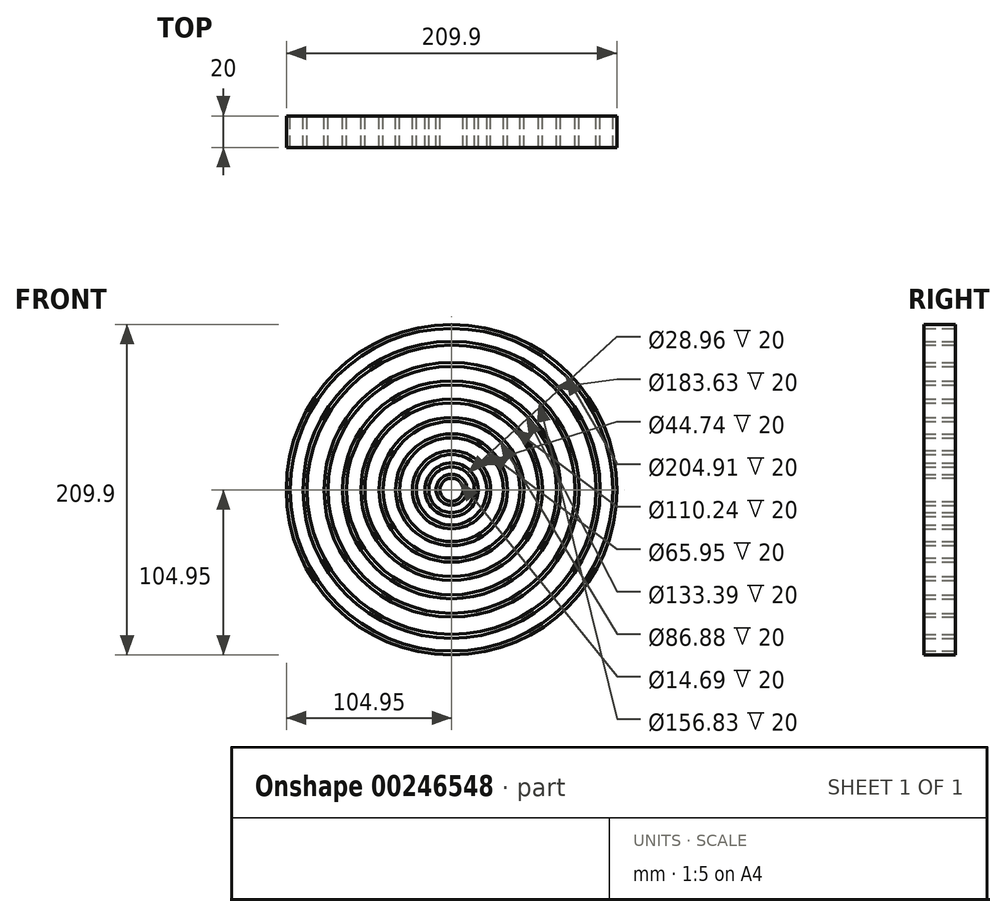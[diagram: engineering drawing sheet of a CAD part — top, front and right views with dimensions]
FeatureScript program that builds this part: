
annotation { "Feature Type Name" : "Feature", "Feature Type Description" : "" }
export const myFeature = defineFeature(function(context is Context, id is Id, definition is map)
    precondition{}
    {
        {
            var Q0;
            Q0=qCreatedBy(makeId("Front.planeOp"),FACE);
            var sketch = newSketch(context, id + "F0", { "sketchPlane" : qUnion([Q0])});
            skCircle(sketch, "E0", {"center": v(0, 0) * mm, "radius": 104.95 * mm});
            skSolve(sketch);
        }
        {
            var Q0;
            Q0=makeQuery(id+"F0.imprint","IMPRINT",FACE,{"disambiguationData":[TD([[makeQuery(id+"F0.imprint","IMPRINT",EDGE,{"derivedFrom":sQuery(id+"F0.wireOp",EDGE,"E0")}),1.0]])]});
            extrude(context, id + "F1", {"entities" : qUnion([Q0]), "endBound" : BoundingType.SYMMETRIC, "depth" : 20 * mm});
        }
        {
            var Q0;
            Q0=makeQuery(id+"F1.opExtrude","CAP_FACE",FACE,{"disambiguationData":[OSD([sQuery(id+"F0.wireOp",EDGE,"E0")])],"isStart":false});
            var Q1;
            Q1=makeQuery(id+"F1.opExtrude","CAP_FACE",FACE,{"disambiguationData":[OSD([sQuery(id+"F0.wireOp",EDGE,"E0")])],"isStart":true});
            shell(context, id + "F2", {"entities" : qUnion([Q0, Q1]), "thickness" : 2.5 * mm});
        }
        {
            var Q0;
            Q0=qCreatedBy(makeId("Front.planeOp"),FACE);
            var sketch = newSketch(context, id + "F3", { "sketchPlane" : qUnion([Q0])});
            skCircle(sketch, "E1", {"center": v(0, 0) * mm, "radius": 94.31 * mm});
            skSolve(sketch);
        }
        {
            var Q0;
            Q0=makeQuery(id+"F3.imprint","IMPRINT",FACE,{"disambiguationData":[TD([[makeQuery(id+"F3.imprint","IMPRINT",EDGE,{"derivedFrom":sQuery(id+"F3.wireOp",EDGE,"E1")}),1.0]])]});
            extrude(context, id + "F4", {"entities" : qUnion([Q0]), "endBound" : BoundingType.SYMMETRIC, "depth" : 20 * mm});
        }
        {
            var Q0;
            Q0=makeQuery(id+"F4.opExtrude","CAP_FACE",FACE,{"disambiguationData":[OSD([sQuery(id+"F3.wireOp",EDGE,"E1")])],"isStart":false});
            var Q1;
            Q1=makeQuery(id+"F4.opExtrude","CAP_FACE",FACE,{"disambiguationData":[OSD([sQuery(id+"F3.wireOp",EDGE,"E1")])],"isStart":true});
            shell(context, id + "F5", {"entities" : qUnion([Q0, Q1]), "thickness" : 2.5 * mm});
        }
        {
            var Q0;
            Q0=qCreatedBy(makeId("Front.planeOp"),FACE);
            var sketch = newSketch(context, id + "F6", { "sketchPlane" : qUnion([Q0])});
            skCircle(sketch, "E2", {"center": v(0, 0) * mm, "radius": 80.91 * mm});
            skSolve(sketch);
        }
        {
            var Q0;
            Q0=makeQuery(id+"F6.imprint","IMPRINT",FACE,{"disambiguationData":[TD([[makeQuery(id+"F6.imprint","IMPRINT",EDGE,{"derivedFrom":sQuery(id+"F6.wireOp",EDGE,"E2")}),1.0]])]});
            extrude(context, id + "F7", {"entities" : qUnion([Q0]), "endBound" : BoundingType.SYMMETRIC, "depth" : 20 * mm});
        }
        {
            var Q0;
            Q0=makeQuery(id+"F7.opExtrude","CAP_FACE",FACE,{"disambiguationData":[OSD([sQuery(id+"F6.wireOp",EDGE,"E2")])],"isStart":false});
            var Q1;
            Q1=makeQuery(id+"F7.opExtrude","CAP_FACE",FACE,{"disambiguationData":[OSD([sQuery(id+"F6.wireOp",EDGE,"E2")])],"isStart":true});
            shell(context, id + "F8", {"entities" : qUnion([Q0, Q1]), "thickness" : 2.5 * mm});
        }
        {
            var Q0;
            Q0=qCreatedBy(makeId("Front.planeOp"),FACE);
            var sketch = newSketch(context, id + "F9", { "sketchPlane" : qUnion([Q0])});
            skCircle(sketch, "E3", {"center": v(0, 0) * mm, "radius": 69.2 * mm});
            skSolve(sketch);
        }
        {
            var Q0;
            Q0=makeQuery(id+"F9.imprint","IMPRINT",FACE,{"disambiguationData":[TD([[makeQuery(id+"F9.imprint","IMPRINT",EDGE,{"derivedFrom":sQuery(id+"F9.wireOp",EDGE,"E3")}),1.0]])]});
            extrude(context, id + "F10", {"entities" : qUnion([Q0]), "endBound" : BoundingType.SYMMETRIC, "depth" : 20 * mm});
        }
        {
            var Q0;
            Q0=makeQuery(id+"F10.opExtrude","CAP_FACE",FACE,{"disambiguationData":[OSD([sQuery(id+"F9.wireOp",EDGE,"E3")])],"isStart":false});
            var Q1;
            Q1=makeQuery(id+"F10.opExtrude","CAP_FACE",FACE,{"disambiguationData":[OSD([sQuery(id+"F9.wireOp",EDGE,"E3")])],"isStart":true});
            shell(context, id + "F11", {"entities" : qUnion([Q0, Q1]), "thickness" : 2.5 * mm});
        }
        {
            var Q0;
            Q0=qCreatedBy(makeId("Front.planeOp"),FACE);
            var sketch = newSketch(context, id + "F12", { "sketchPlane" : qUnion([Q0])});
            skCircle(sketch, "E4", {"center": v(0, 0) * mm, "radius": 57.62 * mm});
            skSolve(sketch);
        }
        {
            var Q0;
            Q0=makeQuery(id+"F12.imprint","IMPRINT",FACE,{"disambiguationData":[TD([[makeQuery(id+"F12.imprint","IMPRINT",EDGE,{"derivedFrom":sQuery(id+"F12.wireOp",EDGE,"E4")}),1.0]])]});
            extrude(context, id + "F13", {"entities" : qUnion([Q0]), "endBound" : BoundingType.SYMMETRIC, "depth" : 20 * mm});
        }
        {
            var Q0;
            Q0=makeQuery(id+"F13.opExtrude","CAP_FACE",FACE,{"disambiguationData":[OSD([sQuery(id+"F12.wireOp",EDGE,"E4")])],"isStart":false});
            var Q1;
            Q1=makeQuery(id+"F13.opExtrude","CAP_FACE",FACE,{"disambiguationData":[OSD([sQuery(id+"F12.wireOp",EDGE,"E4")])],"isStart":true});
            shell(context, id + "F14", {"entities" : qUnion([Q0, Q1]), "thickness" : 2.5 * mm});
        }
        {
            var Q0;
            Q0=qCreatedBy(makeId("Front.planeOp"),FACE);
            var sketch = newSketch(context, id + "F15", { "sketchPlane" : qUnion([Q0])});
            skCircle(sketch, "E5", {"center": v(0, 0) * mm, "radius": 45.94 * mm});
            skSolve(sketch);
        }
        {
            var Q0;
            Q0=makeQuery(id+"F15.imprint","IMPRINT",FACE,{"disambiguationData":[TD([[makeQuery(id+"F15.imprint","IMPRINT",EDGE,{"derivedFrom":sQuery(id+"F15.wireOp",EDGE,"E5")}),1.0]])]});
            extrude(context, id + "F16", {"entities" : qUnion([Q0]), "endBound" : BoundingType.SYMMETRIC, "depth" : 20 * mm});
        }
        {
            var Q0;
            Q0=makeQuery(id+"F16.opExtrude","CAP_FACE",FACE,{"disambiguationData":[OSD([sQuery(id+"F15.wireOp",EDGE,"E5")])],"isStart":false});
            var Q1;
            Q1=makeQuery(id+"F16.opExtrude","CAP_FACE",FACE,{"disambiguationData":[OSD([sQuery(id+"F15.wireOp",EDGE,"E5")])],"isStart":true});
            shell(context, id + "F17", {"entities" : qUnion([Q0, Q1]), "thickness" : 2.5 * mm});
        }
        {
            var Q0;
            Q0=qCreatedBy(makeId("Front.planeOp"),FACE);
            var sketch = newSketch(context, id + "F18", { "sketchPlane" : qUnion([Q0])});
            skCircle(sketch, "E6", {"center": v(0, 0) * mm, "radius": 35.47 * mm});
            skSolve(sketch);
        }
        {
            var Q0;
            Q0=makeQuery(id+"F18.imprint","IMPRINT",FACE,{"disambiguationData":[TD([[makeQuery(id+"F18.imprint","IMPRINT",EDGE,{"derivedFrom":sQuery(id+"F18.wireOp",EDGE,"E6")}),1.0]])]});
            extrude(context, id + "F19", {"entities" : qUnion([Q0]), "endBound" : BoundingType.SYMMETRIC, "depth" : 20 * mm});
        }
        {
            var Q0;
            Q0=makeQuery(id+"F19.opExtrude","CAP_FACE",FACE,{"disambiguationData":[OSD([sQuery(id+"F18.wireOp",EDGE,"E6")])],"isStart":false});
            var Q1;
            Q1=makeQuery(id+"F19.opExtrude","CAP_FACE",FACE,{"disambiguationData":[OSD([sQuery(id+"F18.wireOp",EDGE,"E6")])],"isStart":true});
            shell(context, id + "F20", {"entities" : qUnion([Q0, Q1]), "thickness" : 2.5 * mm});
        }
        {
            var Q0;
            Q0=qCreatedBy(makeId("Front.planeOp"),FACE);
            var sketch = newSketch(context, id + "F21", { "sketchPlane" : qUnion([Q0])});
            skCircle(sketch, "E7", {"center": v(0, 0) * mm, "radius": 24.87 * mm});
            skSolve(sketch);
        }
        {
            var Q0;
            Q0=makeQuery(id+"F21.imprint","IMPRINT",FACE,{"disambiguationData":[TD([[makeQuery(id+"F21.imprint","IMPRINT",EDGE,{"derivedFrom":sQuery(id+"F21.wireOp",EDGE,"E7")}),1.0]])]});
            extrude(context, id + "F22", {"entities" : qUnion([Q0]), "endBound" : BoundingType.SYMMETRIC, "depth" : 20 * mm});
        }
        {
            var Q0;
            Q0=makeQuery(id+"F22.opExtrude","CAP_FACE",FACE,{"disambiguationData":[OSD([sQuery(id+"F21.wireOp",EDGE,"E7")])],"isStart":false});
            var Q1;
            Q1=makeQuery(id+"F22.opExtrude","CAP_FACE",FACE,{"disambiguationData":[OSD([sQuery(id+"F21.wireOp",EDGE,"E7")])],"isStart":true});
            shell(context, id + "F23", {"entities" : qUnion([Q0, Q1]), "thickness" : 2.5 * mm});
        }
        {
            var Q0;
            Q0=qCreatedBy(makeId("Front.planeOp"),FACE);
            var sketch = newSketch(context, id + "F24", { "sketchPlane" : qUnion([Q0])});
            skCircle(sketch, "E8", {"center": v(0, 0) * mm, "radius": 16.98 * mm});
            skSolve(sketch);
        }
        {
            var Q0;
            Q0=makeQuery(id+"F24.imprint","IMPRINT",FACE,{"disambiguationData":[TD([[makeQuery(id+"F24.imprint","IMPRINT",EDGE,{"derivedFrom":sQuery(id+"F24.wireOp",EDGE,"E8")}),1.0]])]});
            extrude(context, id + "F25", {"entities" : qUnion([Q0]), "endBound" : BoundingType.SYMMETRIC, "depth" : 20 * mm});
        }
        {
            var Q0;
            Q0=makeQuery(id+"F25.opExtrude","CAP_FACE",FACE,{"disambiguationData":[OSD([sQuery(id+"F24.wireOp",EDGE,"E8")])],"isStart":false});
            var Q1;
            Q1=makeQuery(id+"F25.opExtrude","CAP_FACE",FACE,{"disambiguationData":[OSD([sQuery(id+"F24.wireOp",EDGE,"E8")])],"isStart":true});
            shell(context, id + "F26", {"entities" : qUnion([Q0, Q1]), "thickness" : 2.5 * mm});
        }
        {
            var Q0;
            Q0=qCreatedBy(makeId("Front.planeOp"),FACE);
            var sketch = newSketch(context, id + "F27", { "sketchPlane" : qUnion([Q0])});
            skCircle(sketch, "E9", {"center": v(0, 0) * mm, "radius": 9.84 * mm});
            skSolve(sketch);
        }
        {
            var Q0;
            Q0=makeQuery(id+"F27.imprint","IMPRINT",FACE,{"disambiguationData":[TD([[makeQuery(id+"F27.imprint","IMPRINT",EDGE,{"derivedFrom":sQuery(id+"F27.wireOp",EDGE,"E9")}),1.0]])]});
            extrude(context, id + "F28", {"entities" : qUnion([Q0]), "endBound" : BoundingType.SYMMETRIC, "depth" : 20 * mm});
        }
        {
            var Q0;
            Q0=makeQuery(id+"F28.opExtrude","CAP_FACE",FACE,{"disambiguationData":[OSD([sQuery(id+"F27.wireOp",EDGE,"E9")])],"isStart":false});
            var Q1;
            Q1=makeQuery(id+"F28.opExtrude","CAP_FACE",FACE,{"disambiguationData":[OSD([sQuery(id+"F27.wireOp",EDGE,"E9")])],"isStart":true});
            shell(context, id + "F29", {"entities" : qUnion([Q0, Q1]), "thickness" : 2.5 * mm});
        }
    });
